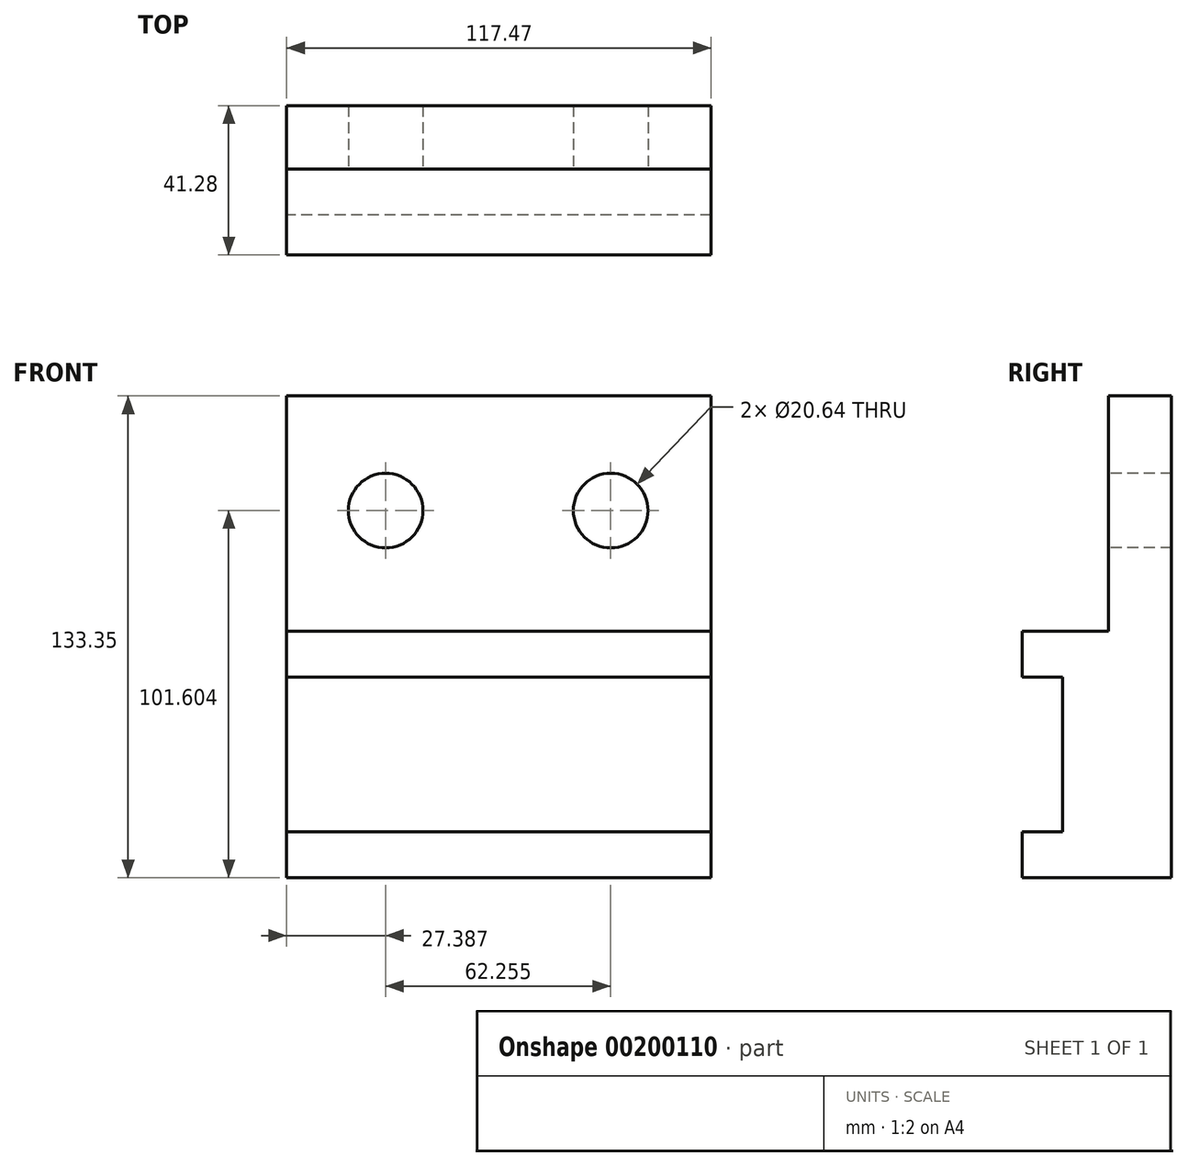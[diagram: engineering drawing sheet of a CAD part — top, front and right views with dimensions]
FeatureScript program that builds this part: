
annotation { "Feature Type Name" : "Feature", "Feature Type Description" : "" }
export const myFeature = defineFeature(function(context is Context, id is Id, definition is map)
    precondition{}
    {
        {
            var Q0;
            Q0=qCreatedBy(makeId("Right.planeOp"),FACE);
            var sketch = newSketch(context, id + "F0", { "sketchPlane" : qUnion([Q0])});
            skLineSegment(sketch, "E0", {"start": v(440.36, 656.12) * mm, "end": v(440.36, 522.77) * mm});
            skLineSegment(sketch, "E1", {"start": v(440.36, 522.77) * mm, "end": v(399.08, 522.77) * mm});
            skLineSegment(sketch, "E2", {"start": v(399.08, 522.77) * mm, "end": v(399.08, 535.47) * mm});
            skLineSegment(sketch, "E3", {"start": v(399.08, 535.47) * mm, "end": v(410.2, 535.47) * mm});
            skLineSegment(sketch, "E4", {"start": v(410.2, 535.47) * mm, "end": v(410.2, 578.34) * mm});
            skLineSegment(sketch, "E5", {"start": v(410.2, 578.34) * mm, "end": v(399.08, 578.34) * mm});
            skLineSegment(sketch, "E6", {"start": v(399.08, 578.34) * mm, "end": v(399.08, 591.04) * mm});
            skLineSegment(sketch, "E7", {"start": v(399.08, 591.04) * mm, "end": v(422.9, 591.04) * mm});
            skLineSegment(sketch, "E8", {"start": v(422.9, 591.04) * mm, "end": v(422.9, 656.12) * mm});
            skLineSegment(sketch, "E9", {"start": v(422.9, 656.12) * mm, "end": v(440.36, 656.12) * mm});
            skSolve(sketch);
        }
        {
            var Q0;
            Q0 = qSketchRegion(id + "F0", true);
            extrude(context, id + "F1", {"entities" : qUnion([Q0]), "depth" : 117.47 * mm});
        }
        {
            var Q0;
            Q0=makeQuery(id+"F1.opExtrude","SWEPT_FACE",FACE,{"disambiguationData":[OSD([sQuery(id+"F0.wireOp",EDGE,"E8")])]});
            var sketch = newSketch(context, id + "F2", { "sketchPlane" : qUnion([Q0])});
            skCircle(sketch, "E10", {"center": v(27.39, 624.37) * mm, "radius": 10.32 * mm});
            skCircle(sketch, "E11", {"center": v(89.64, 624.37) * mm, "radius": 10.32 * mm});
            skSolve(sketch);
        }
        {
            var Q0;
            Q0=makeQuery(id+"F2.imprint","IMPRINT",FACE,{"disambiguationData":[TD([[makeQuery(id+"F2.imprint","IMPRINT",EDGE,{"derivedFrom":sQuery(id+"F2.wireOp",EDGE,"E10")}),1.0]])]});
            var Q1;
            Q1=makeQuery(id+"F2.imprint","IMPRINT",FACE,{"disambiguationData":[TD([[makeQuery(id+"F2.imprint","IMPRINT",EDGE,{"derivedFrom":sQuery(id+"F2.wireOp",EDGE,"E11")}),1.0]])]});
            extrude(context, id + "F3", {"entities" : qUnion([Q0, Q1]), "operationType" : NewBodyOperationType.REMOVE, "endBound" : BoundingType.THROUGH_ALL, "oppositeDirection" : true, "depth" : 25.4 * mm});
        }
    });
